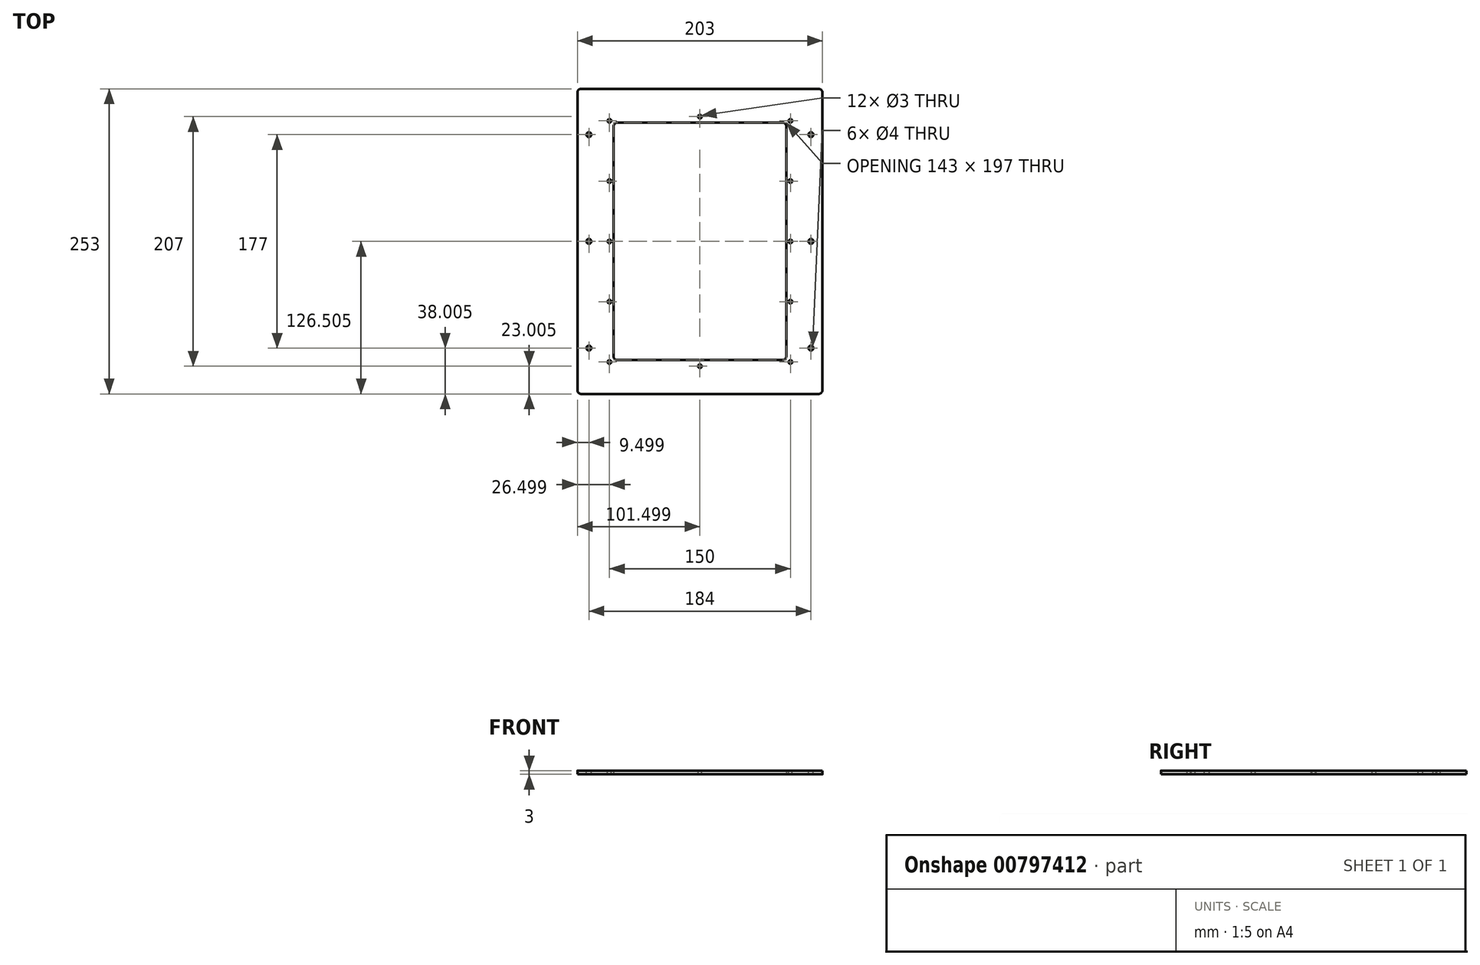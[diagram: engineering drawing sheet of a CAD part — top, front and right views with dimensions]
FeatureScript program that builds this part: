
annotation { "Feature Type Name" : "Feature", "Feature Type Description" : "" }
export const myFeature = defineFeature(function(context is Context, id is Id, definition is map)
    precondition{}
    {
        {
            var Q0;
            Q0=qCreatedBy(makeId("Top.planeOp"),FACE);
            var sketch = newSketch(context, id + "F0", { "sketchPlane" : qUnion([Q0])});
            skLineSegment(sketch, "E0.bottom", {"start": v(-116.38, -25.9) * mm, "end": v(80.62, -25.9) * mm});
            skLineSegment(sketch, "E0.top", {"start": v(-116.38, -278.9) * mm, "end": v(80.62, -278.9) * mm});
            skLineSegment(sketch, "E0.left", {"start": v(-119.38, -28.9) * mm, "end": v(-119.38, -275.9) * mm});
            skLineSegment(sketch, "E0.right", {"start": v(83.62, -28.9) * mm, "end": v(83.62, -275.9) * mm});
            skPoint(sketch, "E1.visualSharp", {"position": v(-119.38, -25.9) * mm});
            skArc(sketch, "E1.filletArc", {"start": v(-116.38, -25.9) * mm, "mid": v(-118.5, -26.78) * mm, "end": v(-119.38, -28.9) * mm});
            skPoint(sketch, "E2.visualSharp", {"position": v(83.62, -25.9) * mm});
            skArc(sketch, "E2.filletArc", {"start": v(83.62, -28.9) * mm, "mid": v(82.74, -26.78) * mm, "end": v(80.62, -25.9) * mm});
            skPoint(sketch, "E3.visualSharp", {"position": v(-119.38, -278.9) * mm});
            skArc(sketch, "E3.filletArc", {"start": v(-119.38, -275.9) * mm, "mid": v(-118.5, -278.03) * mm, "end": v(-116.38, -278.9) * mm});
            skPoint(sketch, "E4.visualSharp", {"position": v(83.62, -278.9) * mm});
            skArc(sketch, "E4.filletArc", {"start": v(80.62, -278.9) * mm, "mid": v(82.74, -278.03) * mm, "end": v(83.62, -275.9) * mm});
            skLineSegment(sketch, "E5.bottom", {"start": v(-86.38, -53.9) * mm, "end": v(50.62, -53.9) * mm});
            skLineSegment(sketch, "E5.top", {"start": v(-86.38, -250.9) * mm, "end": v(50.62, -250.9) * mm});
            skLineSegment(sketch, "E5.left", {"start": v(-89.38, -56.9) * mm, "end": v(-89.38, -247.9) * mm});
            skLineSegment(sketch, "E5.right", {"start": v(53.62, -56.9) * mm, "end": v(53.62, -247.9) * mm});
            skPoint(sketch, "E6.visualSharp", {"position": v(-89.38, -53.9) * mm});
            skArc(sketch, "E6.filletArc", {"start": v(-86.38, -53.9) * mm, "mid": v(-88.5, -54.78) * mm, "end": v(-89.38, -56.9) * mm});
            skPoint(sketch, "E7.visualSharp", {"position": v(53.62, -53.9) * mm});
            skArc(sketch, "E7.filletArc", {"start": v(53.62, -56.9) * mm, "mid": v(52.74, -54.78) * mm, "end": v(50.62, -53.9) * mm});
            skPoint(sketch, "E8.visualSharp", {"position": v(-89.38, -250.9) * mm});
            skArc(sketch, "E8.filletArc", {"start": v(-89.38, -247.9) * mm, "mid": v(-88.5, -250.03) * mm, "end": v(-86.38, -250.9) * mm});
            skPoint(sketch, "E9.visualSharp", {"position": v(53.62, -250.9) * mm});
            skArc(sketch, "E9.filletArc", {"start": v(50.62, -250.9) * mm, "mid": v(52.74, -250.03) * mm, "end": v(53.62, -247.9) * mm});
            skSolve(sketch);
        }
        {
            var Q0;
            Q0 = qSketchRegion(id + "F0", true);
            extrude(context, id + "F1", {"entities" : qUnion([Q0]), "depth" : 3 * mm, "offsetDistance" : 25 * mm});
        }
        {
            var Q0;
            Q0=makeQuery(id+"F1.opExtrude","CAP_FACE",FACE,{"disambiguationData":[OSD([sQuery(id+"F0.wireOp",EDGE,"E0.bottom"),sQuery(id+"F0.wireOp",EDGE,"E0.top"),sQuery(id+"F0.wireOp",EDGE,"E0.left"),sQuery(id+"F0.wireOp",EDGE,"E0.right"),sQuery(id+"F0.wireOp",EDGE,"E1.filletArc"),sQuery(id+"F0.wireOp",EDGE,"E2.filletArc"),sQuery(id+"F0.wireOp",EDGE,"E3.filletArc"),sQuery(id+"F0.wireOp",EDGE,"E4.filletArc"),sQuery(id+"F0.wireOp",EDGE,"E5.bottom"),sQuery(id+"F0.wireOp",EDGE,"E5.top"),sQuery(id+"F0.wireOp",EDGE,"E5.left"),sQuery(id+"F0.wireOp",EDGE,"E5.right"),sQuery(id+"F0.wireOp",EDGE,"E6.filletArc"),sQuery(id+"F0.wireOp",EDGE,"E7.filletArc"),sQuery(id+"F0.wireOp",EDGE,"E8.filletArc"),sQuery(id+"F0.wireOp",EDGE,"E9.filletArc")])],"isStart":false});
            var sketch = newSketch(context, id + "F2", { "sketchPlane" : qUnion([Q0])});
            skLineSegment(sketch, "E10.bottom", {"start": v(-109.88, -63.9) * mm, "end": v(74.12, -63.9) * mm, "construction": true});
            skLineSegment(sketch, "E10.top", {"start": v(-109.88, -240.9) * mm, "end": v(74.12, -240.9) * mm, "construction": true});
            skLineSegment(sketch, "E10.left", {"start": v(-109.88, -63.9) * mm, "end": v(-109.88, -240.9) * mm, "construction": true});
            skLineSegment(sketch, "E10.right", {"start": v(74.12, -63.9) * mm, "end": v(74.12, -240.9) * mm, "construction": true});
            skLineSegment(sketch, "E11", {"start": v(-109.88, -152.4) * mm, "end": v(74.12, -152.4) * mm, "construction": true});
            skCircle(sketch, "E12", {"center": v(-109.88, -63.9) * mm, "radius": 2 * mm});
            skCircle(sketch, "E13", {"center": v(74.12, -63.9) * mm, "radius": 2 * mm});
            skCircle(sketch, "E14", {"center": v(74.12, -152.4) * mm, "radius": 2 * mm});
            skCircle(sketch, "E15", {"center": v(74.12, -240.9) * mm, "radius": 2 * mm});
            skCircle(sketch, "E16", {"center": v(-109.88, -240.9) * mm, "radius": 2 * mm});
            skCircle(sketch, "E17", {"center": v(-109.88, -152.4) * mm, "radius": 2 * mm});
            skSolve(sketch);
        }
        {
            var Q0;
            Q0 = qSketchRegion(id + "F2", true);
            extrude(context, id + "F3", {"entities" : qUnion([Q0]), "operationType" : NewBodyOperationType.REMOVE, "oppositeDirection" : true, "depth" : 25 * mm, "offsetDistance" : 25 * mm});
        }
        {
            var Q0;
            Q0=makeQuery(id+"F1.opExtrude","CAP_FACE",FACE,{"disambiguationData":[OSD([sQuery(id+"F0.wireOp",EDGE,"E0.bottom"),sQuery(id+"F0.wireOp",EDGE,"E0.top"),sQuery(id+"F0.wireOp",EDGE,"E0.left"),sQuery(id+"F0.wireOp",EDGE,"E0.right"),sQuery(id+"F0.wireOp",EDGE,"E1.filletArc"),sQuery(id+"F0.wireOp",EDGE,"E2.filletArc"),sQuery(id+"F0.wireOp",EDGE,"E3.filletArc"),sQuery(id+"F0.wireOp",EDGE,"E4.filletArc"),sQuery(id+"F0.wireOp",EDGE,"E5.bottom"),sQuery(id+"F0.wireOp",EDGE,"E5.top"),sQuery(id+"F0.wireOp",EDGE,"E5.left"),sQuery(id+"F0.wireOp",EDGE,"E5.right"),sQuery(id+"F0.wireOp",EDGE,"E6.filletArc"),sQuery(id+"F0.wireOp",EDGE,"E7.filletArc"),sQuery(id+"F0.wireOp",EDGE,"E8.filletArc"),sQuery(id+"F0.wireOp",EDGE,"E9.filletArc")])],"isStart":false});
            var sketch = newSketch(context, id + "F4", { "sketchPlane" : qUnion([Q0])});
            skLineSegment(sketch, "E18.bottom", {"start": v(-92.88, -52.4) * mm, "end": v(57.12, -52.4) * mm, "construction": true});
            skLineSegment(sketch, "E18.top", {"start": v(-92.88, -252.4) * mm, "end": v(57.12, -252.4) * mm, "construction": true});
            skLineSegment(sketch, "E18.left", {"start": v(-92.88, -52.4) * mm, "end": v(-92.88, -252.4) * mm, "construction": true});
            skLineSegment(sketch, "E18.right", {"start": v(57.12, -52.4) * mm, "end": v(57.12, -252.4) * mm, "construction": true});
            skLineSegment(sketch, "E19", {"start": v(-92.88, -152.4) * mm, "end": v(57.12, -152.4) * mm, "construction": true});
            skLineSegment(sketch, "E20", {"start": v(-17.88, -52.4) * mm, "end": v(-17.88, -48.9) * mm});
            skLineSegment(sketch, "E21", {"start": v(-17.88, -252.4) * mm, "end": v(-17.88, -255.9) * mm});
            skLineSegment(sketch, "E22", {"start": v(-92.88, -202.4) * mm, "end": v(57.12, -202.4) * mm, "construction": true});
            skLineSegment(sketch, "E23", {"start": v(-92.88, -102.4) * mm, "end": v(57.12, -102.4) * mm, "construction": true});
            skCircle(sketch, "E24", {"center": v(-92.88, -52.4) * mm, "radius": 1.5 * mm});
            skCircle(sketch, "E25", {"center": v(-17.88, -48.9) * mm, "radius": 1.5 * mm});
            skCircle(sketch, "E26", {"center": v(57.12, -52.4) * mm, "radius": 1.5 * mm});
            skCircle(sketch, "E27", {"center": v(57.12, -102.4) * mm, "radius": 1.5 * mm});
            skCircle(sketch, "E28", {"center": v(-92.88, -102.4) * mm, "radius": 1.5 * mm});
            skCircle(sketch, "E29", {"center": v(57.12, -152.4) * mm, "radius": 1.5 * mm});
            skCircle(sketch, "E30", {"center": v(-92.88, -152.4) * mm, "radius": 1.5 * mm});
            skCircle(sketch, "E31", {"center": v(-92.88, -202.4) * mm, "radius": 1.5 * mm});
            skCircle(sketch, "E32", {"center": v(57.12, -202.4) * mm, "radius": 1.5 * mm});
            skCircle(sketch, "E33", {"center": v(-92.88, -252.4) * mm, "radius": 1.5 * mm});
            skCircle(sketch, "E34", {"center": v(-17.88, -255.9) * mm, "radius": 1.5 * mm});
            skCircle(sketch, "E35", {"center": v(57.12, -252.4) * mm, "radius": 1.5 * mm});
            skSolve(sketch);
        }
        {
            var Q0;
            Q0 = qSketchRegion(id + "F4", true);
            extrude(context, id + "F5", {"entities" : qUnion([Q0]), "operationType" : NewBodyOperationType.REMOVE, "oppositeDirection" : true, "depth" : 25 * mm, "offsetDistance" : 25 * mm});
        }
    });
